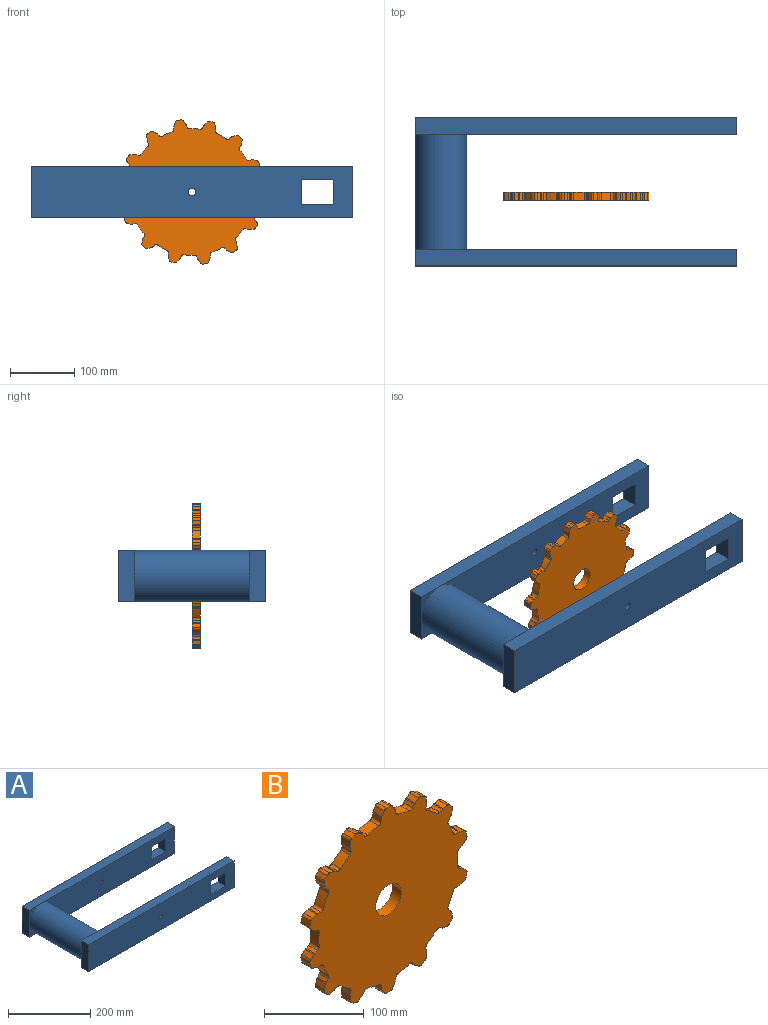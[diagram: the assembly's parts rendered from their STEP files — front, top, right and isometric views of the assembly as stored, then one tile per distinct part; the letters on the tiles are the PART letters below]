
ASSEMBLY  parts=2 mates=1
PART A: 27 faces, bbox 500x230x80 mm
  f0: plane 460x80mm, normal (0,1,0), area 32173.6mm2, adj f4,f8,f9,f10,f21,f22,f23,f24
  f1: plane 500x80mm, normal (0,-1,0), area 37886.9mm2, adj f7,f8,f9,f10,f21,f22,f23,f24
  f2: plane 460x80mm, normal (0,-1,0), area 32173.6mm2, adj f4,f14,f15,f16,f17,f18,f19,f20
  f3: plane 500x80mm, normal (0,1,0), area 37886.9mm2, adj f13,f14,f15,f16,f17,f18,f19,f20
  f4: cylinder r=40mm len=180mm, axis (0,1,0), area 45238.9mm2, adj f0,f2,f5,f6,f11,f12
  f5: plane 40x40mm, normal (0,1,0), area 343.4mm2, adj f4,f7,f10
  f6: plane 40x40mm, normal (0,1,0), area 343.4mm2, adj f4,f7,f8
  f7: plane 80x25mm, normal (-1,0,0), area 2000mm2, adj f1,f5,f6,f8,f10
  f8: plane 500x25mm, normal (0,0,-1), area 12500mm2, adj f0,f1,f6,f7,f9
  f9: plane 80x25mm, normal (1,0,0), area 2000mm2, adj f0,f1,f8,f10
  f10: plane 500x25mm, normal (0,0,1), area 12500mm2, adj f0,f1,f5,f7,f9
  f11: plane 40x40mm, normal (0,-1,0), area 343.4mm2, adj f4,f13,f16
  f12: plane 40x40mm, normal (0,-1,0), area 343.4mm2, adj f4,f13,f14
  f13: plane 80x25mm, normal (-1,0,0), area 2000mm2, adj f3,f11,f12,f14,f16
  f14: plane 500x25mm, normal (0,0,-1), area 12500mm2, adj f2,f3,f12,f13,f15
  f15: plane 80x25mm, normal (1,0,0), area 2000mm2, adj f2,f3,f14,f16
  f16: plane 500x25mm, normal (0,0,1), area 12500mm2, adj f2,f3,f11,f13,f15
  f17: plane 50x25mm, normal (0,0,1), area 1250mm2, adj f2,f3,f18,f20
  f18: plane 40x25mm, normal (1,0,0), area 1000mm2, adj f2,f3,f17,f19
  f19: plane 50x25mm, normal (0,0,-1), area 1250mm2, adj f2,f3,f18,f20
  f20: plane 40x25mm, normal (-1,0,0), area 1000mm2, adj f2,f3,f17,f19
  f21: plane 40x25mm, normal (-1,0,0), area 1000mm2, adj f0,f1,f22,f24
  f22: plane 50x25mm, normal (0,0,-1), area 1250mm2, adj f0,f1,f21,f23
  f23: plane 40x25mm, normal (1,0,0), area 1000mm2, adj f0,f1,f22,f24
  f24: plane 50x25mm, normal (0,0,1), area 1250mm2, adj f0,f1,f21,f23
  f25: cylinder r=6mm len=25mm, axis (0,-1,0), area 942.5mm2, adj f2,f3
  f26: cylinder r=6mm len=25mm, axis (0,-1,0), area 942.5mm2, adj f0,f1
PART B: 171 faces, bbox 222.6x12.5x227 mm
  f0: cylinder r=98.5mm len=16.07mm, axis (0,-1,0), area 206.3mm2, adj f14,f15,f25,f103
  f1: cylinder r=98.5mm len=16.07mm, axis (0,-1,0), area 206.3mm2, adj f14,f15,f23,f114
  f2: cylinder r=98.5mm len=12.89mm, axis (0,-1,0), area 206.3mm2, adj f14,f15,f113,f125
  f3: cylinder r=98.5mm len=14.85mm, axis (0,-1,0), area 206.3mm2, adj f14,f15,f124,f136
  f4: cylinder r=98.5mm len=16.48mm, axis (0,-1,0), area 206.3mm2, adj f14,f15,f135,f147
  f5: cylinder r=98.5mm len=14.85mm, axis (0,-1,0), area 206.3mm2, adj f14,f15,f146,f158
  f6: cylinder r=98.5mm len=12.89mm, axis (0,-1,0), area 206.3mm2, adj f14,f15,f157,f168
  f7: cylinder r=98.5mm len=16.07mm, axis (0,-1,0), area 206.3mm2, adj f14,f15,f37,f166
  f8: cylinder r=98.5mm len=16.07mm, axis (0,-1,0), area 206.3mm2, adj f14,f15,f36,f48
  f9: cylinder r=98.5mm len=12.89mm, axis (0,-1,0), area 206.3mm2, adj f14,f15,f47,f59
  f10: cylinder r=98.5mm len=14.85mm, axis (0,-1,0), area 206.3mm2, adj f14,f15,f58,f70
  f11: cylinder r=98.5mm len=16.48mm, axis (0,-1,0), area 206.3mm2, adj f14,f15,f69,f81
  f12: cylinder r=98.5mm len=14.85mm, axis (0,-1,0), area 206.3mm2, adj f14,f15,f80,f92
  f13: cylinder r=98.5mm len=12.89mm, axis (0,-1,0), area 206.3mm2, adj f14,f15,f91,f102
  f14: plane 227x222.62mm, normal (0,1,0), area 33153.6mm2, adj f0,f1,f2,f3,f4,f5,f6,f7
  f15: plane 227x222.62mm, normal (0,-1,0), area 33153.6mm2, adj f0,f1,f2,f3,f4,f5,f6,f7
  f16: plane 12.5x4.14mm, normal (0.98,0,0.19), area 52.8mm2, adj f14,f15,f25,f26
  f17: plane 12.5x5.38mm, normal (0.87,0,0.5), area 77.5mm2, adj f14,f15,f24,f26
  f18: cylinder r=113.5mm len=12.5mm, axis (0,-1,0), area 68.2mm2, adj f14,f15,f21,f24
  f19: plane 12.5x5.38mm, normal (-0.87,0,0.5), area 77.5mm2, adj f14,f15,f21,f22
  f20: plane 12.5x4.14mm, normal (-0.98,0,0.19), area 52.8mm2, adj f14,f15,f22,f23
  f21: cylinder r=4mm len=12.5mm, axis (0,-1,0), area 51.4mm2, adj f14,f15,f18,f19
  f22: cylinder r=4mm len=12.5mm, axis (0,-1,0), area 16.2mm2, adj f14,f15,f19,f20
  f23: cylinder r=4mm len=12.5mm, axis (0,-1,0), area 61.8mm2, adj f1,f14,f15,f20
  f24: cylinder r=4mm len=12.5mm, axis (0,-1,0), area 51.4mm2, adj f14,f15,f17,f18
  f25: cylinder r=4mm len=12.5mm, axis (0,-1,0), area 61.8mm2, adj f0,f14,f15,f16
  f26: cylinder r=4mm len=12.5mm, axis (0,-1,0), area 16.2mm2, adj f14,f15,f16,f17
  f27: plane 12.5x4.14mm, normal (0.98,0,-0.19), area 52.8mm2, adj f14,f15,f28,f36
  f28: cylinder r=4mm len=12.5mm, axis (0,-1,0), area 16.2mm2, adj f14,f15,f27,f29
  f29: plane 12.5x5.38mm, normal (0.87,0,-0.5), area 77.5mm2, adj f14,f15,f28,f30
  f30: cylinder r=4mm len=12.5mm, axis (0,-1,0), area 51.4mm2, adj f14,f15,f29,f31
  f31: cylinder r=113.5mm len=12.5mm, axis (0,-1,0), area 68.2mm2, adj f14,f15,f30,f32
  f32: cylinder r=4mm len=12.5mm, axis (0,-1,0), area 51.4mm2, adj f14,f15,f31,f33
  f33: plane 12.5x5.38mm, normal (-0.87,0,-0.5), area 77.5mm2, adj f14,f15,f32,f34
  f34: cylinder r=4mm len=12.5mm, axis (0,-1,0), area 16.2mm2, adj f14,f15,f33,f35
  f35: plane 12.5x4.14mm, normal (-0.98,0,-0.19), area 52.8mm2, adj f14,f15,f34,f37
  f36: cylinder r=4mm len=12.5mm, axis (0,-1,0), area 61.8mm2, adj f8,f14,f15,f27
  f37: cylinder r=4mm len=12.5mm, axis (0,-1,0), area 61.8mm2, adj f7,f14,f15,f35
  f38: plane 12.5x4.09mm, normal (0.97,0,0.25), area 52.8mm2, adj f14,f15,f39,f47
  f39: cylinder r=4mm len=12.5mm, axis (0,-1,0), area 16.2mm2, adj f14,f15,f38,f40
  f40: plane 12.5x6.18mm, normal (1,0,-0.07), area 77.5mm2, adj f14,f15,f39,f41
  f41: cylinder r=4mm len=12.5mm, axis (0,-1,0), area 51.4mm2, adj f14,f15,f40,f42
  f42: cylinder r=113.5mm len=12.5mm, axis (0,-1,0), area 68.2mm2, adj f14,f15,f41,f43
  f43: cylinder r=4mm len=12.5mm, axis (0,-1,0), area 51.4mm2, adj f14,f15,f42,f44
  f44: plane 12.5x5.1mm, normal (-0.57,0,-0.82), area 77.5mm2, adj f14,f15,f43,f45
  f45: cylinder r=4mm len=12.5mm, axis (0,-1,0), area 16.2mm2, adj f14,f15,f44,f46
  f46: plane 12.5x3.38mm, normal (-0.8,0,-0.6), area 52.8mm2, adj f14,f15,f45,f48
  f47: cylinder r=4mm len=12.5mm, axis (0,-1,0), area 61.8mm2, adj f9,f14,f15,f38
  f48: cylinder r=4mm len=12.5mm, axis (0,-1,0), area 61.8mm2, adj f8,f14,f15,f46
  f49: plane 12.5x3.22mm, normal (0.76,0,0.65), area 52.8mm2, adj f14,f15,f50,f58
  f50: cylinder r=4mm len=12.5mm, axis (0,-1,0), area 16.2mm2, adj f14,f15,f49,f51
  f51: plane 12.5x5.76mm, normal (0.93,0,0.37), area 77.5mm2, adj f14,f15,f50,f52
  f52: cylinder r=4mm len=12.5mm, axis (0,-1,0), area 51.4mm2, adj f14,f15,f51,f53
  f53: cylinder r=113.5mm len=12.5mm, axis (0,-1,0), area 68.2mm2, adj f14,f15,f52,f54
  f54: cylinder r=4mm len=12.5mm, axis (0,-1,0), area 51.4mm2, adj f14,f15,f53,f55
  f55: plane 12.5x6.12mm, normal (-0.15,0,-0.99), area 77.5mm2, adj f14,f15,f54,f56
  f56: cylinder r=4mm len=12.5mm, axis (0,-1,0), area 16.2mm2, adj f14,f15,f55,f57
  f57: plane 12.5x3.75mm, normal (-0.46,0,-0.89), area 52.8mm2, adj f14,f15,f56,f59
  f58: cylinder r=4mm len=12.5mm, axis (0,-1,0), area 61.8mm2, adj f10,f14,f15,f49
  f59: cylinder r=4mm len=12.5mm, axis (0,-1,0), area 61.8mm2, adj f9,f14,f15,f57
  f60: plane 12.5x3.86mm, normal (0.41,0,0.91), area 52.8mm2, adj f14,f15,f61,f69
  f61: cylinder r=4mm len=12.5mm, axis (0,-1,0), area 16.2mm2, adj f14,f15,f60,f62
  f62: plane 12.5x4.56mm, normal (0.68,0,0.74), area 77.5mm2, adj f14,f15,f61,f63
  f63: cylinder r=4mm len=12.5mm, axis (0,-1,0), area 51.4mm2, adj f14,f15,f62,f64
  f64: cylinder r=113.5mm len=12.5mm, axis (0,-1,0), area 68.2mm2, adj f14,f15,f63,f65
  f65: cylinder r=4mm len=12.5mm, axis (0,-1,0), area 51.4mm2, adj f14,f15,f64,f66
  f66: plane 12.5x5.93mm, normal (0.29,0,-0.96), area 77.5mm2, adj f14,f15,f65,f67
  f67: cylinder r=4mm len=12.5mm, axis (0,-1,0), area 16.2mm2, adj f14,f15,f66,f68
  f68: plane 12.5x4.22mm, normal (-0.03,0,-1), area 52.8mm2, adj f14,f15,f67,f70
  f69: cylinder r=4mm len=12.5mm, axis (0,-1,0), area 61.8mm2, adj f11,f14,f15,f60
  f70: cylinder r=4mm len=12.5mm, axis (0,-1,0), area 61.8mm2, adj f10,f14,f15,f68
  f71: plane 12.5x4.22mm, normal (-0.03,0,1), area 52.8mm2, adj f14,f15,f72,f80
  f72: cylinder r=4mm len=12.5mm, axis (0,-1,0), area 16.2mm2, adj f14,f15,f71,f73
  f73: plane 12.5x5.93mm, normal (0.29,0,0.96), area 77.5mm2, adj f14,f15,f72,f74
  f74: cylinder r=4mm len=12.5mm, axis (0,-1,0), area 51.4mm2, adj f14,f15,f73,f75
  f75: cylinder r=113.5mm len=12.5mm, axis (0,-1,0), area 68.2mm2, adj f14,f15,f74,f76
  f76: cylinder r=4mm len=12.5mm, axis (0,-1,0), area 51.4mm2, adj f14,f15,f75,f77
  f77: plane 12.5x4.56mm, normal (0.68,0,-0.74), area 77.5mm2, adj f14,f15,f76,f78
  f78: cylinder r=4mm len=12.5mm, axis (0,-1,0), area 16.2mm2, adj f14,f15,f77,f79
  f79: plane 12.5x3.86mm, normal (0.41,0,-0.91), area 52.8mm2, adj f14,f15,f78,f81
  f80: cylinder r=4mm len=12.5mm, axis (0,-1,0), area 61.8mm2, adj f12,f14,f15,f71
  f81: cylinder r=4mm len=12.5mm, axis (0,-1,0), area 61.8mm2, adj f11,f14,f15,f79
  f82: plane 12.5x3.75mm, normal (-0.46,0,0.89), area 52.8mm2, adj f14,f15,f83,f91
  f83: cylinder r=4mm len=12.5mm, axis (0,-1,0), area 16.2mm2, adj f14,f15,f82,f84
  f84: plane 12.5x6.12mm, normal (-0.15,0,0.99), area 77.5mm2, adj f14,f15,f83,f85
  f85: cylinder r=4mm len=12.5mm, axis (0,-1,0), area 51.4mm2, adj f14,f15,f84,f86
  f86: cylinder r=113.5mm len=12.5mm, axis (0,-1,0), area 68.2mm2, adj f14,f15,f85,f87
  f87: cylinder r=4mm len=12.5mm, axis (0,-1,0), area 51.4mm2, adj f14,f15,f86,f88
  f88: plane 12.5x5.76mm, normal (0.93,0,-0.37), area 77.5mm2, adj f14,f15,f87,f89
  f89: cylinder r=4mm len=12.5mm, axis (0,-1,0), area 16.2mm2, adj f14,f15,f88,f90
  f90: plane 12.5x3.22mm, normal (0.76,0,-0.65), area 52.8mm2, adj f14,f15,f89,f92
  f91: cylinder r=4mm len=12.5mm, axis (0,-1,0), area 61.8mm2, adj f13,f14,f15,f82
  f92: cylinder r=4mm len=12.5mm, axis (0,-1,0), area 61.8mm2, adj f12,f14,f15,f90
  f93: plane 12.5x3.38mm, normal (-0.8,0,0.6), area 52.8mm2, adj f14,f15,f94,f103
  f94: cylinder r=4mm len=12.5mm, axis (0,-1,0), area 16.2mm2, adj f14,f15,f93,f95
  f95: plane 12.5x5.1mm, normal (-0.57,0,0.82), area 77.5mm2, adj f14,f15,f94,f96
  f96: cylinder r=4mm len=12.5mm, axis (0,-1,0), area 51.4mm2, adj f14,f15,f95,f97
  f97: cylinder r=113.5mm len=12.5mm, axis (0,-1,0), area 68.2mm2, adj f14,f15,f96,f98
  f98: cylinder r=4mm len=12.5mm, axis (0,-1,0), area 51.4mm2, adj f14,f15,f97,f99
  f99: plane 12.5x6.18mm, normal (1,0,0.07), area 77.5mm2, adj f14,f15,f98,f100
  f100: cylinder r=4mm len=12.5mm, axis (0,-1,0), area 16.2mm2, adj f14,f15,f99,f101
  f101: plane 12.5x4.09mm, normal (0.97,0,-0.25), area 52.8mm2, adj f14,f15,f100,f102
  f102: cylinder r=4mm len=12.5mm, axis (0,-1,0), area 61.8mm2, adj f13,f14,f15,f101
  f103: cylinder r=4mm len=12.5mm, axis (0,-1,0), area 61.8mm2, adj f0,f14,f15,f93
  f104: plane 12.5x4.09mm, normal (-0.97,0,-0.25), area 52.8mm2, adj f14,f15,f105,f113
  f105: cylinder r=4mm len=12.5mm, axis (0,-1,0), area 16.2mm2, adj f14,f15,f104,f106
  f106: plane 12.5x6.18mm, normal (-1,0,0.07), area 77.5mm2, adj f14,f15,f105,f107
  f107: cylinder r=4mm len=12.5mm, axis (0,-1,0), area 51.4mm2, adj f14,f15,f106,f108
  f108: cylinder r=113.5mm len=12.5mm, axis (0,-1,0), area 68.2mm2, adj f14,f15,f107,f109
  f109: cylinder r=4mm len=12.5mm, axis (0,-1,0), area 51.4mm2, adj f14,f15,f108,f110
  f110: plane 12.5x5.1mm, normal (0.57,0,0.82), area 77.5mm2, adj f14,f15,f109,f111
  f111: cylinder r=4mm len=12.5mm, axis (0,-1,0), area 16.2mm2, adj f14,f15,f110,f112
  f112: plane 12.5x3.38mm, normal (0.8,0,0.6), area 52.8mm2, adj f14,f15,f111,f114
  f113: cylinder r=4mm len=12.5mm, axis (0,-1,0), area 61.8mm2, adj f2,f14,f15,f104
  f114: cylinder r=4mm len=12.5mm, axis (0,-1,0), area 61.8mm2, adj f1,f14,f15,f112
  f115: plane 12.5x3.22mm, normal (-0.76,0,-0.65), area 52.8mm2, adj f14,f15,f116,f124
  f116: cylinder r=4mm len=12.5mm, axis (0,-1,0), area 16.2mm2, adj f14,f15,f115,f117
  f117: plane 12.5x5.76mm, normal (-0.93,0,-0.37), area 77.5mm2, adj f14,f15,f116,f118
  f118: cylinder r=4mm len=12.5mm, axis (0,-1,0), area 51.4mm2, adj f14,f15,f117,f119
  f119: cylinder r=113.5mm len=12.5mm, axis (0,-1,0), area 68.2mm2, adj f14,f15,f118,f120
  f120: cylinder r=4mm len=12.5mm, axis (0,-1,0), area 51.4mm2, adj f14,f15,f119,f121
  f121: plane 12.5x6.12mm, normal (0.15,0,0.99), area 77.5mm2, adj f14,f15,f120,f122
  f122: cylinder r=4mm len=12.5mm, axis (0,-1,0), area 16.2mm2, adj f14,f15,f121,f123
  f123: plane 12.5x3.75mm, normal (0.46,0,0.89), area 52.8mm2, adj f14,f15,f122,f125
  f124: cylinder r=4mm len=12.5mm, axis (0,-1,0), area 61.8mm2, adj f3,f14,f15,f115
  f125: cylinder r=4mm len=12.5mm, axis (0,-1,0), area 61.8mm2, adj f2,f14,f15,f123
  f126: plane 12.5x3.86mm, normal (-0.41,0,-0.91), area 52.8mm2, adj f14,f15,f127,f135
  f127: cylinder r=4mm len=12.5mm, axis (0,-1,0), area 16.2mm2, adj f14,f15,f126,f128
  f128: plane 12.5x4.56mm, normal (-0.68,0,-0.74), area 77.5mm2, adj f14,f15,f127,f129
  f129: cylinder r=4mm len=12.5mm, axis (0,-1,0), area 51.4mm2, adj f14,f15,f128,f130
  f130: cylinder r=113.5mm len=12.5mm, axis (0,-1,0), area 68.2mm2, adj f14,f15,f129,f131
  f131: cylinder r=4mm len=12.5mm, axis (0,-1,0), area 51.4mm2, adj f14,f15,f130,f132
  f132: plane 12.5x5.93mm, normal (-0.29,0,0.96), area 77.5mm2, adj f14,f15,f131,f133
  f133: cylinder r=4mm len=12.5mm, axis (0,-1,0), area 16.2mm2, adj f14,f15,f132,f134
  f134: plane 12.5x4.22mm, normal (0.03,0,1), area 52.8mm2, adj f14,f15,f133,f136
  f135: cylinder r=4mm len=12.5mm, axis (0,-1,0), area 61.8mm2, adj f4,f14,f15,f126
  f136: cylinder r=4mm len=12.5mm, axis (0,-1,0), area 61.8mm2, adj f3,f14,f15,f134
  f137: plane 12.5x4.22mm, normal (0.03,0,-1), area 52.8mm2, adj f14,f15,f138,f146
  f138: cylinder r=4mm len=12.5mm, axis (0,-1,0), area 16.2mm2, adj f14,f15,f137,f139
  f139: plane 12.5x5.93mm, normal (-0.29,0,-0.96), area 77.5mm2, adj f14,f15,f138,f140
  f140: cylinder r=4mm len=12.5mm, axis (0,-1,0), area 51.4mm2, adj f14,f15,f139,f141
  f141: cylinder r=113.5mm len=12.5mm, axis (0,-1,0), area 68.2mm2, adj f14,f15,f140,f142
  f142: cylinder r=4mm len=12.5mm, axis (0,-1,0), area 51.4mm2, adj f14,f15,f141,f143
  f143: plane 12.5x4.56mm, normal (-0.68,0,0.74), area 77.5mm2, adj f14,f15,f142,f144
  f144: cylinder r=4mm len=12.5mm, axis (0,-1,0), area 16.2mm2, adj f14,f15,f143,f145
  f145: plane 12.5x3.86mm, normal (-0.41,0,0.91), area 52.8mm2, adj f14,f15,f144,f147
  f146: cylinder r=4mm len=12.5mm, axis (0,-1,0), area 61.8mm2, adj f5,f14,f15,f137
  f147: cylinder r=4mm len=12.5mm, axis (0,-1,0), area 61.8mm2, adj f4,f14,f15,f145
  f148: plane 12.5x3.75mm, normal (0.46,0,-0.89), area 52.8mm2, adj f14,f15,f149,f157
  f149: cylinder r=4mm len=12.5mm, axis (0,-1,0), area 16.2mm2, adj f14,f15,f148,f150
  f150: plane 12.5x6.12mm, normal (0.15,0,-0.99), area 77.5mm2, adj f14,f15,f149,f151
  f151: cylinder r=4mm len=12.5mm, axis (0,-1,0), area 51.4mm2, adj f14,f15,f150,f152
  f152: cylinder r=113.5mm len=12.5mm, axis (0,-1,0), area 68.2mm2, adj f14,f15,f151,f153
  f153: cylinder r=4mm len=12.5mm, axis (0,-1,0), area 51.4mm2, adj f14,f15,f152,f154
  f154: plane 12.5x5.76mm, normal (-0.93,0,0.37), area 77.5mm2, adj f14,f15,f153,f155
  f155: cylinder r=4mm len=12.5mm, axis (0,-1,0), area 16.2mm2, adj f14,f15,f154,f156
  f156: plane 12.5x3.22mm, normal (-0.76,0,0.65), area 52.8mm2, adj f14,f15,f155,f158
  f157: cylinder r=4mm len=12.5mm, axis (0,-1,0), area 61.8mm2, adj f6,f14,f15,f148
  f158: cylinder r=4mm len=12.5mm, axis (0,-1,0), area 61.8mm2, adj f5,f14,f15,f156
  f159: plane 12.5x4.09mm, normal (-0.97,0,0.25), area 52.8mm2, adj f14,f15,f168,f169
  f160: plane 12.5x6.18mm, normal (-1,0,-0.07), area 77.5mm2, adj f14,f15,f167,f169
  f161: cylinder r=113.5mm len=12.5mm, axis (0,-1,0), area 68.2mm2, adj f14,f15,f164,f167
  f162: plane 12.5x5.1mm, normal (0.57,0,-0.82), area 77.5mm2, adj f14,f15,f164,f165
  f163: plane 12.5x3.38mm, normal (0.8,0,-0.6), area 52.8mm2, adj f14,f15,f165,f166
  f164: cylinder r=4mm len=12.5mm, axis (0,-1,0), area 51.4mm2, adj f14,f15,f161,f162
  f165: cylinder r=4mm len=12.5mm, axis (0,-1,0), area 16.2mm2, adj f14,f15,f162,f163
  f166: cylinder r=4mm len=12.5mm, axis (0,-1,0), area 61.8mm2, adj f7,f14,f15,f163
  f167: cylinder r=4mm len=12.5mm, axis (0,-1,0), area 51.4mm2, adj f14,f15,f160,f161
  f168: cylinder r=4mm len=12.5mm, axis (0,-1,0), area 61.8mm2, adj f6,f14,f15,f159
  f169: cylinder r=4mm len=12.5mm, axis (0,-1,0), area 16.2mm2, adj f14,f15,f159,f160
  f170: cylinder r=18mm len=36mm, axis (0,-1,0), area 1413.7mm2, adj f14,f15
PLACE A t=(-195.83,115,-21.03)mm fixed
PLACE B rot(axis=(0,-1,0),87.4deg) t=(14.17,114.56,-21.03)mm
MATE cylindrical B.f170 <-> A.f25  axis (0,-1,0) through (14.17,102.06,-21.03)mm
